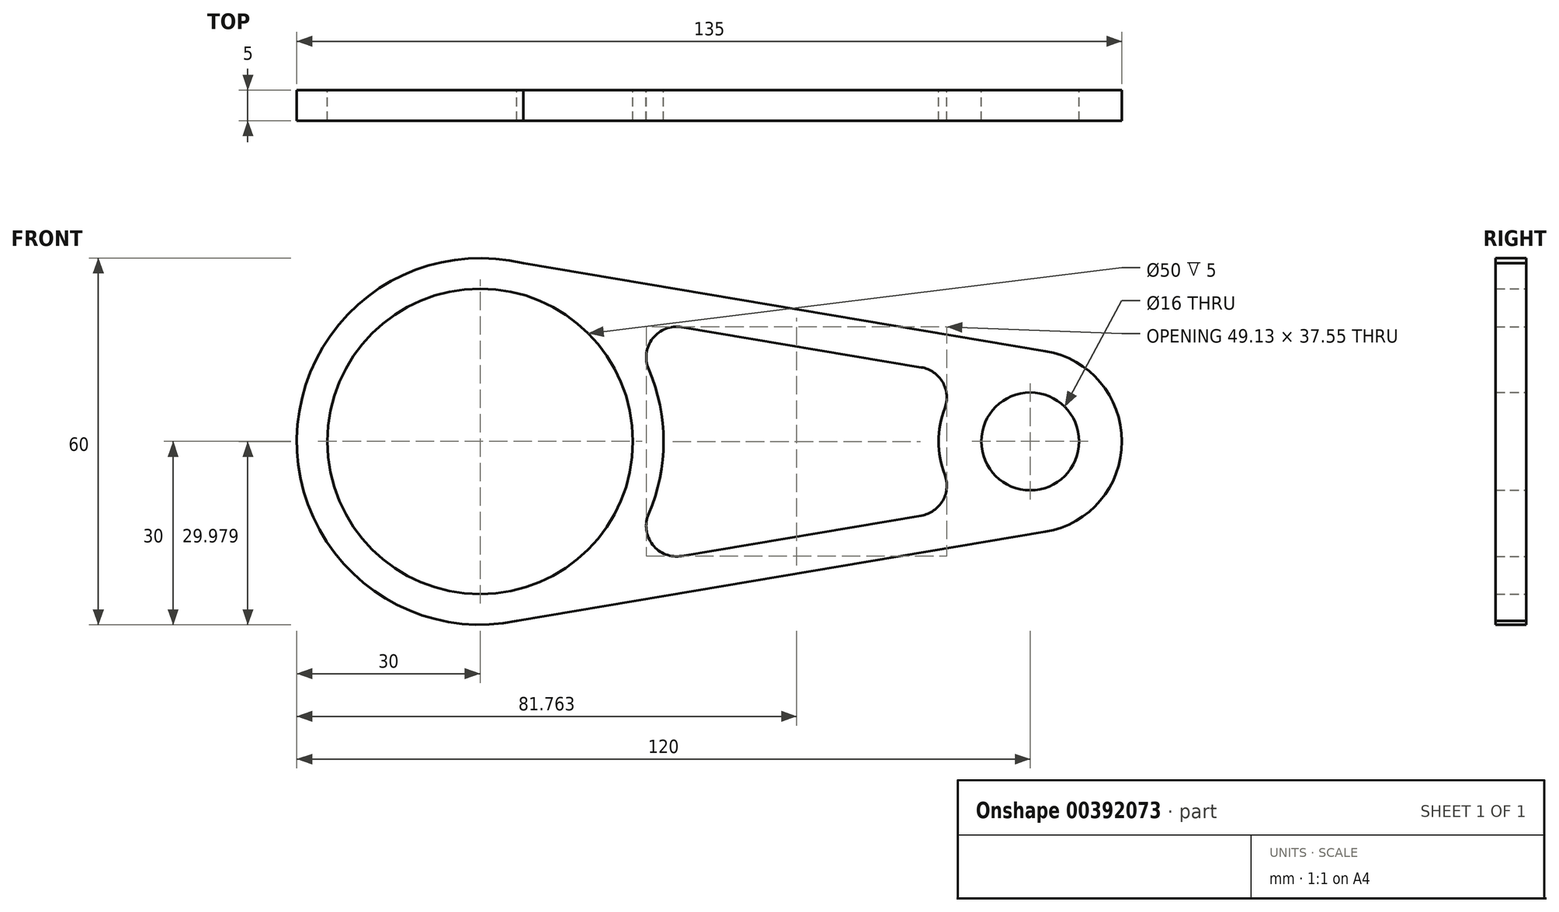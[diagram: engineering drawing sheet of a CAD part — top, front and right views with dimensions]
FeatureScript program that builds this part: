
annotation { "Feature Type Name" : "Feature", "Feature Type Description" : "" }
export const myFeature = defineFeature(function(context is Context, id is Id, definition is map)
    precondition{}
    {
        {
            var Q0;
            Q0=qCreatedBy(makeId("Front.planeOp"),FACE);
            var sketch = newSketch(context, id + "F0", { "sketchPlane" : qUnion([Q0])});
            skCircle(sketch, "E0", {"center": v(0, 0) * mm, "radius": 25 * mm});
            skArc(sketch, "E1", {"start": v(7.04, 29.16) * mm, "mid": v(-30, 0.53) * mm, "end": v(6, -29.4) * mm});
            skArc(sketch, "E2", {"start": v(92.5, -14.8) * mm, "mid": v(105, 0) * mm, "end": v(92.49, 14.8) * mm});
            skCircle(sketch, "E3", {"center": v(90, 0) * mm, "radius": 8 * mm});
            skLineSegment(sketch, "E4", {"start": v(2.89, 29.86) * mm, "end": v(92.49, 14.8) * mm});
            skLineSegment(sketch, "E5", {"start": v(6, -29.4) * mm, "end": v(92.5, -14.8) * mm});
            skLineSegment(sketch, "E6", {"start": v(33, 18.71) * mm, "end": v(72.17, 12.13) * mm});
            skLineSegment(sketch, "E7", {"start": v(32.99, -18.75) * mm, "end": v(72.18, -12.14) * mm});
            skArc(sketch, "E8.trimOffspring", {"start": v(27.56, -11.85) * mm, "mid": v(30, -0.02) * mm, "end": v(27.58, 11.81) * mm});
            skArc(sketch, "E9.trimOffspring", {"start": v(76, 5.4) * mm, "mid": v(75, 0) * mm, "end": v(76, -5.4) * mm});
            skPoint(sketch, "E10.visualSharp", {"position": v(21.82, 20.6) * mm});
            skArc(sketch, "E10.filletArc", {"start": v(33, 18.71) * mm, "mid": v(28.24, 16.87) * mm, "end": v(27.58, 11.81) * mm});
            skPoint(sketch, "E11.visualSharp", {"position": v(21.76, -20.65) * mm});
            skArc(sketch, "E11.filletArc", {"start": v(27.56, -11.85) * mm, "mid": v(28.22, -16.91) * mm, "end": v(32.99, -18.75) * mm});
            skPoint(sketch, "E12.visualSharp", {"position": v(79.67, -10.87) * mm});
            skArc(sketch, "E12.filletArc", {"start": v(72.18, -12.14) * mm, "mid": v(75.69, -9.68) * mm, "end": v(76, -5.4) * mm});
            skPoint(sketch, "E13.visualSharp", {"position": v(79.66, 10.87) * mm});
            skArc(sketch, "E13.filletArc", {"start": v(76, 5.4) * mm, "mid": v(75.68, 9.67) * mm, "end": v(72.17, 12.13) * mm});
            skSolve(sketch);
        }
        {
            var Q0;
            Q0 = qSketchRegion(id + "F0", true);
            extrude(context, id + "F1", {"entities" : qUnion([Q0]), "depth" : 5 * mm});
        }
    });
